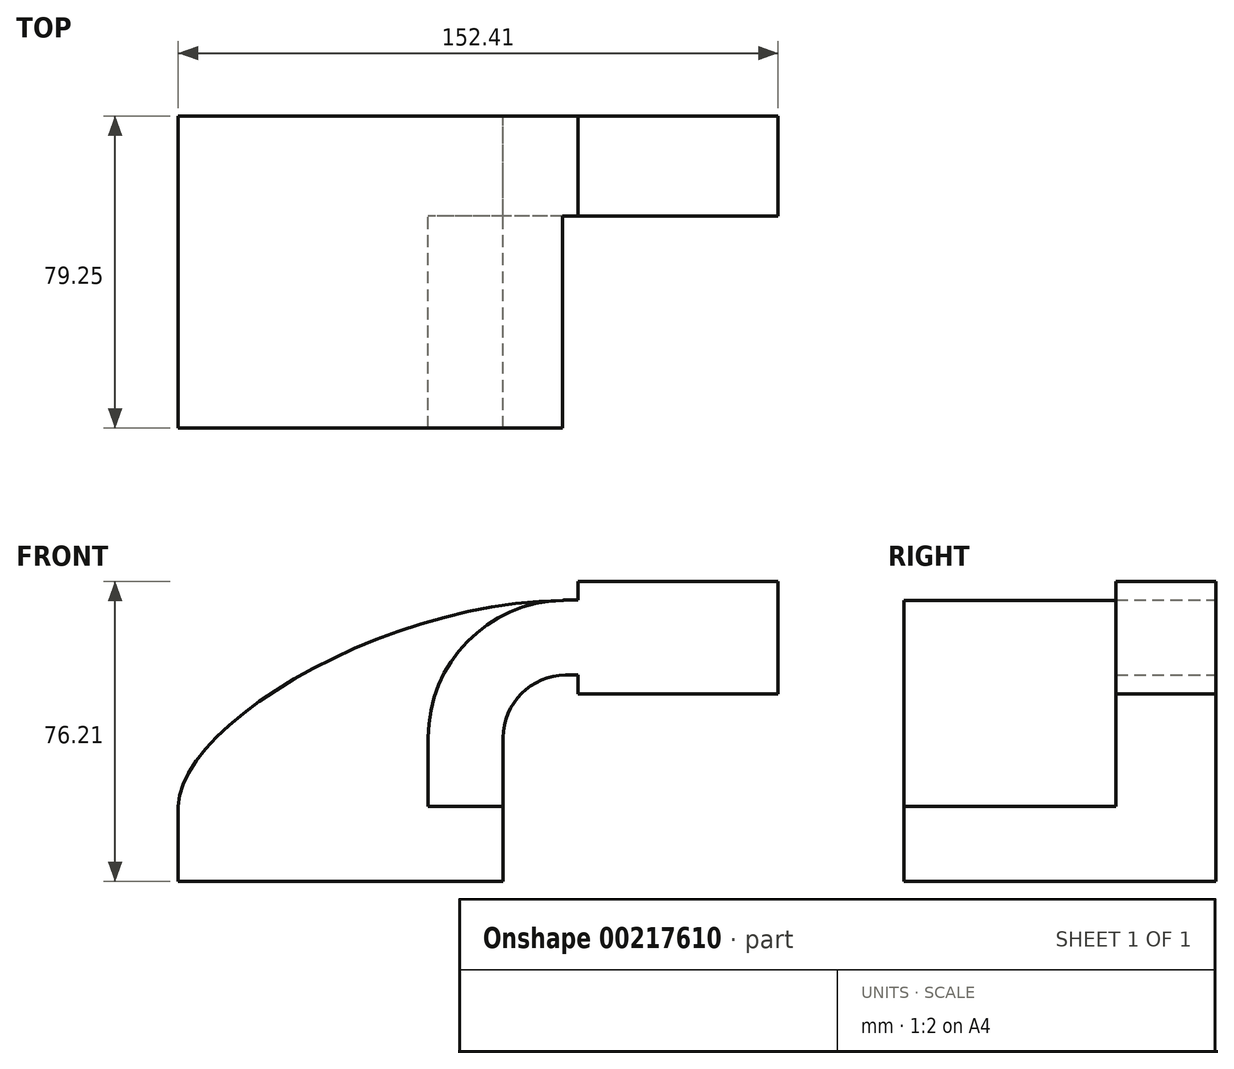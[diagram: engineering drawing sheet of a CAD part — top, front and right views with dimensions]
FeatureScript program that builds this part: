
annotation { "Feature Type Name" : "Feature", "Feature Type Description" : "" }
export const myFeature = defineFeature(function(context is Context, id is Id, definition is map)
    precondition{}
    {
        {
            var Q0;
            Q0=qCreatedBy(makeId("Front.planeOp"),FACE);
            var sketch = newSketch(context, id + "F0", { "sketchPlane" : qUnion([Q0])});
            skLineSegment(sketch, "E0.bottom", {"start": v(41.27, 9.53) * mm, "end": v(-41.28, 9.53) * mm});
            skLineSegment(sketch, "E0.top", {"start": v(41.28, -9.52) * mm, "end": v(-41.27, -9.52) * mm});
            skLineSegment(sketch, "E0.left", {"start": v(41.28, 9.53) * mm, "end": v(41.28, -9.52) * mm});
            skLineSegment(sketch, "E0.right", {"start": v(-41.28, 9.53) * mm, "end": v(-41.27, -9.52) * mm});
            skPoint(sketch, "E0.middle", {"position": v(0, 0) * mm});
            skLineSegment(sketch, "E1.bottom", {"start": v(111.12, 66.68) * mm, "end": v(60.33, 66.68) * mm});
            skLineSegment(sketch, "E1.top", {"start": v(111.13, 38.1) * mm, "end": v(60.33, 38.1) * mm});
            skLineSegment(sketch, "E1.left", {"start": v(111.12, 66.68) * mm, "end": v(111.13, 38.1) * mm});
            skLineSegment(sketch, "E1.right", {"start": v(60.33, 66.68) * mm, "end": v(60.33, 38.1) * mm});
            skPoint(sketch, "E1.middle", {"position": v(85.73, 52.39) * mm});
            skLineSegment(sketch, "E2", {"start": v(41.27, 9.53) * mm, "end": v(41.27, 27) * mm});
            skArc(sketch, "E3", {"start": v(41.27, 27) * mm, "mid": v(45.92, 38.23) * mm, "end": v(57.15, 42.88) * mm});
            skLineSegment(sketch, "E4", {"start": v(57.15, 42.88) * mm, "end": v(85.73, 42.88) * mm});
            skLineSegment(sketch, "E5.0", {"start": v(57.15, 61.93) * mm, "end": v(85.73, 61.93) * mm});
            skArc(sketch, "E5.1", {"start": v(22.23, 27) * mm, "mid": v(32.45, 51.7) * mm, "end": v(57.15, 61.93) * mm});
            skLineSegment(sketch, "E5.2", {"start": v(22.23, 9.53) * mm, "end": v(22.23, 27) * mm});
            skLineSegment(sketch, "E6", {"start": v(85.73, 61.93) * mm, "end": v(85.73, 42.88) * mm});
            skFitSpline(sketch, "E7", {"points": [v(-41.28, 9.53) * mm, v(57.15, 61.93) * mm], "startDerivative": vector(0.94, 62.62) * mm, "endDerivative": vector(137.44, 1.03) * mm});
            skSolve(sketch);
        }
        {
            var Q0;
            Q0=makeQuery(id+"F0.imprint","IMPRINT",FACE,{"disambiguationData":[TD([[makeQuery(id+"F0.imprint","IMPRINT",EDGE,{"derivedFrom":sQuery(id+"F0.wireOp",EDGE,"E0.top")}),-1.0]])]});
            var sketch = newSketch(context, id + "F1", { "sketchPlane" : qUnion([Q0])});
            skSolve(sketch);
        }
        {
            var Q0;
            Q0=makeQuery(id+"F0.imprint","IMPRINT",FACE,{"disambiguationData":[TD([[makeQuery(id+"F0.imprint","IMPRINT",EDGE,{"derivedFrom":sQuery(id+"F0.wireOp",EDGE,"E0.top")}),-1.0]])]});
            var Q1;
            {var subQ3=sQuery(id+"F0.wireOp",EDGE,"E5.2");Q1=makeQuery(id+"F0.imprint","IMPRINT",FACE,{"disambiguationData":[TD([[makeQuery(id+"F0.imprint","IMPRINT",EDGE,{"derivedFrom":subQ3}),1.0]])]});}
            var Q2;
            Q2 = qSketchRegion(id + "F1", true);
            extrude(context, id + "F2", {"entities" : qUnion([Q0, Q1, Q2]), "depth" : 79.25 * mm});
        }
        {
            var Q0;
            Q0 = qSketchRegion(id + "F0", true);
            extrude(context, id + "F3", {"entities" : qUnion([Q0]), "operationType" : NewBodyOperationType.ADD, "depth" : 25.4 * mm});
        }
    });
